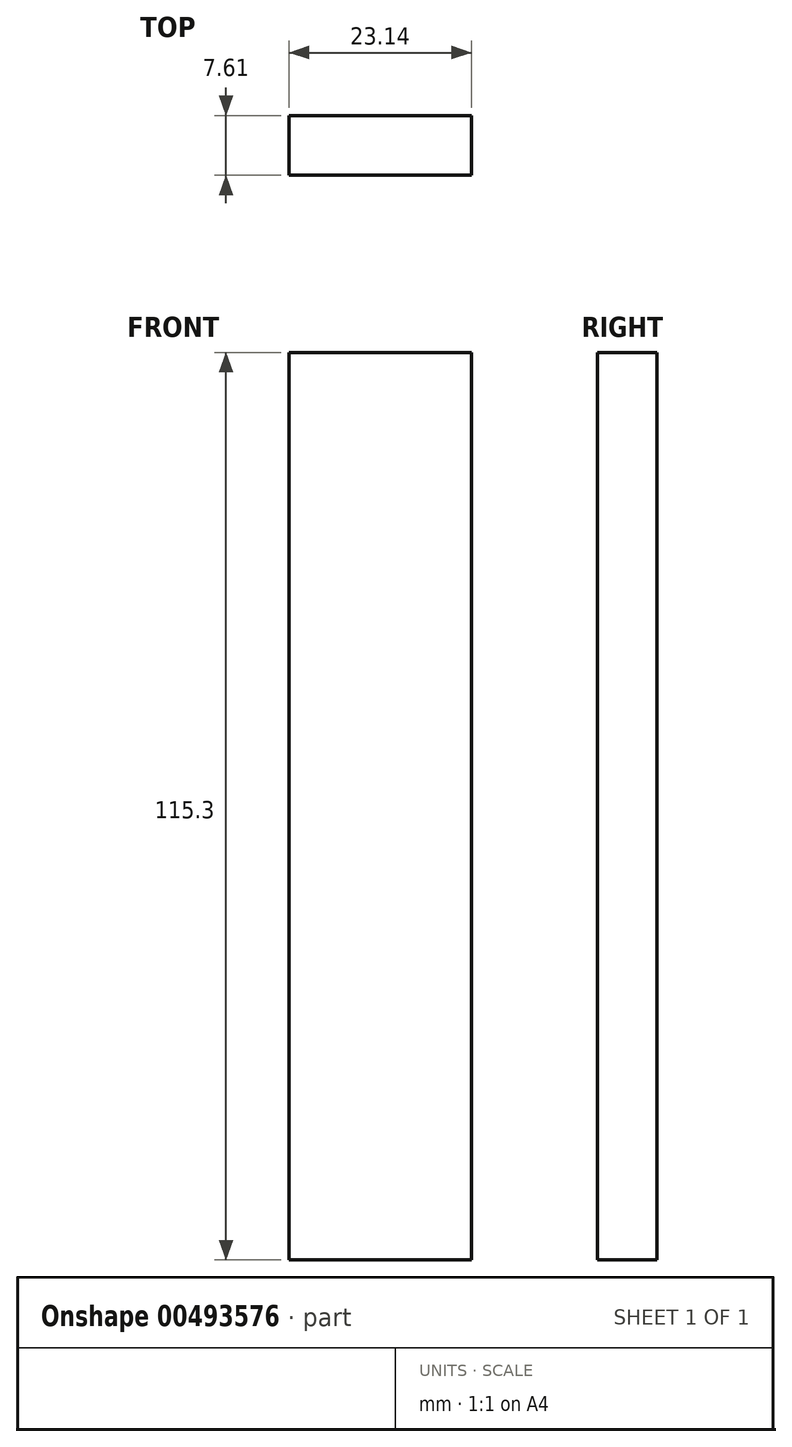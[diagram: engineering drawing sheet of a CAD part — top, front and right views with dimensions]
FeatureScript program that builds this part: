
annotation { "Feature Type Name" : "Feature", "Feature Type Description" : "" }
export const myFeature = defineFeature(function(context is Context, id is Id, definition is map)
    precondition{}
    {
        {
            var Q0;
            Q0=qCreatedBy(makeId("Front.planeOp"),FACE);
            var sketch = newSketch(context, id + "F0", { "sketchPlane" : qUnion([Q0])});
            skLineSegment(sketch, "E0.bottom", {"start": v(11.57, -57.65) * mm, "end": v(-11.57, -57.65) * mm});
            skLineSegment(sketch, "E0.top", {"start": v(11.57, 57.65) * mm, "end": v(-11.57, 57.65) * mm});
            skLineSegment(sketch, "E0.left", {"start": v(11.57, -57.65) * mm, "end": v(11.57, 57.65) * mm});
            skLineSegment(sketch, "E0.right", {"start": v(-11.57, -57.65) * mm, "end": v(-11.57, 57.65) * mm});
            skPoint(sketch, "E0.middle", {"position": v(0, 0) * mm});
            skSolve(sketch);
        }
        {
            var Q0;
            Q0=makeQuery(id+"F0.imprint","IMPRINT",FACE,{"disambiguationData":[TD([[makeQuery(id+"F0.imprint","IMPRINT",EDGE,{"derivedFrom":sQuery(id+"F0.wireOp",EDGE,"E0.bottom")}),-1.0]])]});
            extrude(context, id + "F1", {"entities" : qUnion([Q0]), "depth" : 7.61 * mm});
        }
    });
